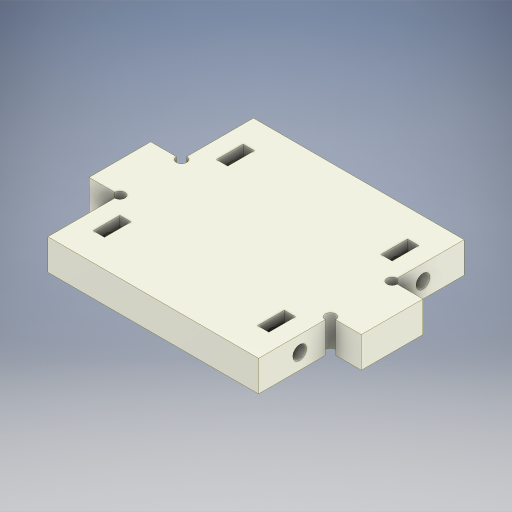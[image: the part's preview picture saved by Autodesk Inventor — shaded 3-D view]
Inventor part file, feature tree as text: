
AUTODESK INVENTOR PART (.ipt)
format: ipt  version: 2024 (Build 280153000, 153)  size: 347,648 bytes
history: native  units: in
note: dims shown in document units (in); Inventor stores cm internally (conversion verified against a paired STEP export)
features: extrude x6, sketch x6, other x3, projected_geometry x1
ambient origin geometry x4: Origin, X Axis, Y Axis, Z Axis
bodies: Body1 (feature_tree)
feature tree (16):
  extrude  "돌출3"  Depth=1.6142in
  extrude  "돌출4"  Depth=1.1811in
  extrude  "돌출5"  Depth=0.2362in
  extrude  "돌출6"  Depth=0.4724in
  extrude  "돌출7"  Depth=0.2362in
  extrude  "돌출9"  Depth=0.4724in
  other  "우측면도"
  other  "평면도"
  other  "정면도"
  sketch  "스케치1"
  sketch  "스케치3"
  sketch  "스케치4"
  sketch  "스케치5"
  sketch  "스케치6"
  sketch  "스케치7"
  projected_geometry  "투영된 루프1"
